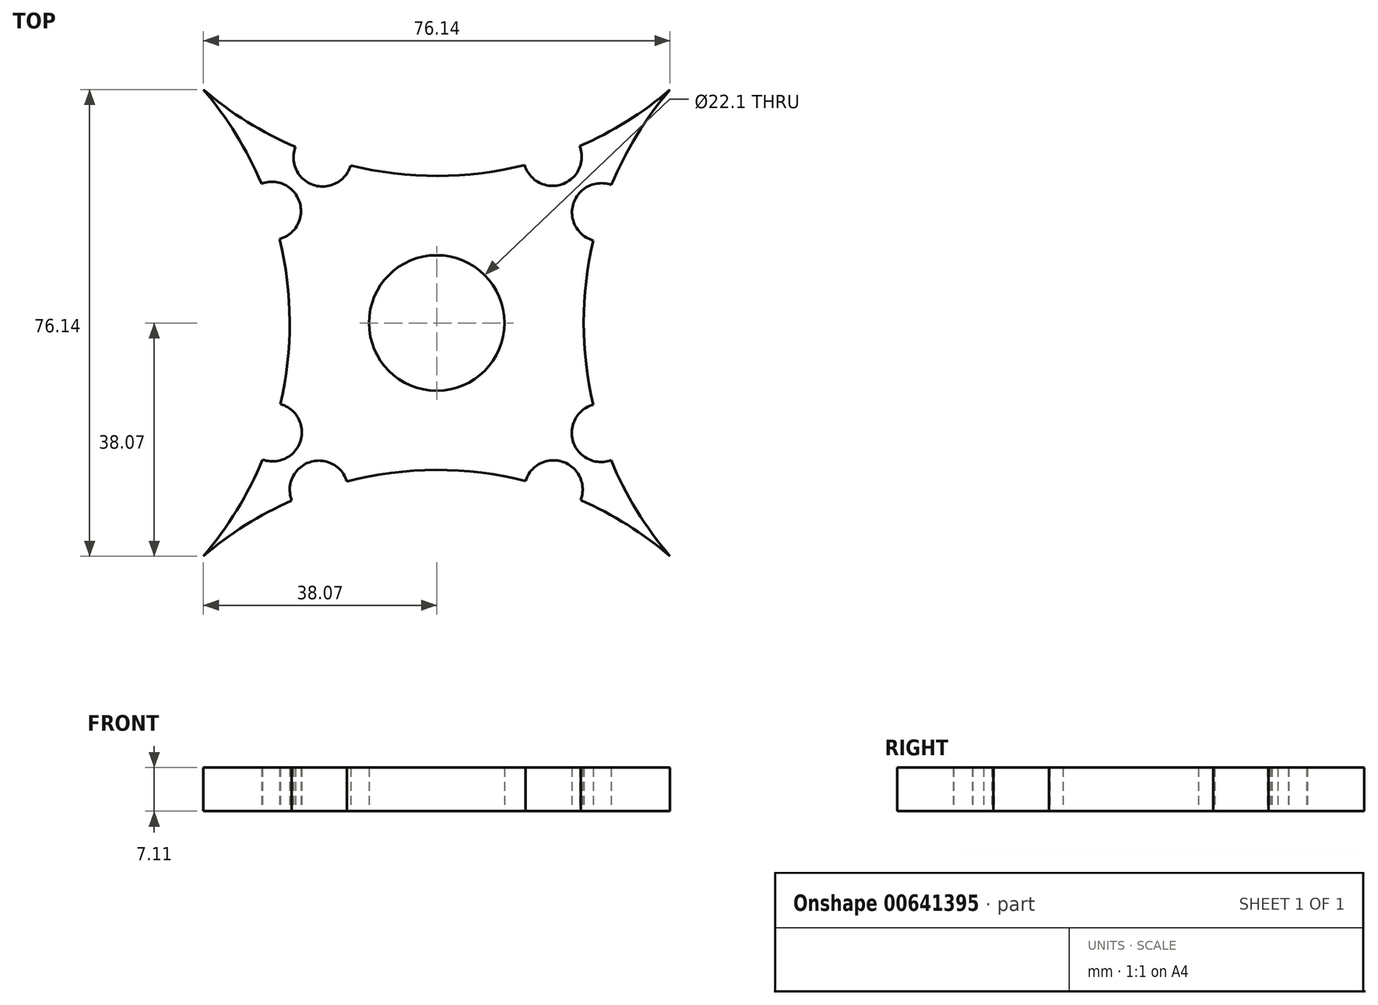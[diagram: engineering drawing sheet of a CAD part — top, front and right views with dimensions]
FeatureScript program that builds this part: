
annotation { "Feature Type Name" : "Feature", "Feature Type Description" : "" }
export const myFeature = defineFeature(function(context is Context, id is Id, definition is map)
    precondition{}
    {
        {
            var Q0;
            Q0=qCreatedBy(makeId("Top.planeOp"),FACE);
            var sketch = newSketch(context, id + "F0", { "sketchPlane" : qUnion([Q0])});
            skCircle(sketch, "E0", {"center": v(0, 0) * mm, "radius": 11.05 * mm});
            skLineSegment(sketch, "E1.bottom", {"start": v(-44.41, 44.41) * mm, "end": v(44.41, 44.41) * mm});
            skLineSegment(sketch, "E1.top", {"start": v(-44.41, -44.41) * mm, "end": v(44.41, -44.41) * mm});
            skLineSegment(sketch, "E1.left", {"start": v(-44.41, 44.41) * mm, "end": v(-44.41, -44.41) * mm});
            skLineSegment(sketch, "E1.right", {"start": v(44.41, 44.41) * mm, "end": v(44.41, -44.41) * mm});
            skArc(sketch, "E2", {"start": v(-44.41, 44.41) * mm, "mid": v(-34.64, 35.35) * mm, "end": v(-23.06, 28.73) * mm});
            skArc(sketch, "E3", {"start": v(44.41, 44.41) * mm, "mid": v(35.17, 34.4) * mm, "end": v(28.5, 22.5) * mm});
            skArc(sketch, "E4", {"start": v(44.41, -44.41) * mm, "mid": v(34.82, -35.48) * mm, "end": v(23.49, -28.91) * mm});
            skArc(sketch, "E5", {"start": v(-44.41, -44.41) * mm, "mid": v(-35.1, -34.3) * mm, "end": v(-28.4, -22.3) * mm});
            skArc(sketch, "E6", {"start": v(-25.61, 13.7) * mm, "mid": v(-22.4, 19.76) * mm, "end": v(-28.59, 22.73) * mm});
            skArc(sketch, "E7", {"start": v(-23.06, 28.73) * mm, "mid": v(-20.13, 22.51) * mm, "end": v(-14.04, 25.7) * mm});
            skArc(sketch, "E8", {"start": v(-28.4, -22.3) * mm, "mid": v(-22.23, -19.28) * mm, "end": v(-25.5, -13.24) * mm});
            skArc(sketch, "E9", {"start": v(-14.66, -25.85) * mm, "mid": v(-20.78, -22.74) * mm, "end": v(-23.64, -28.98) * mm});
            skArc(sketch, "E10", {"start": v(23.49, -28.91) * mm, "mid": v(20.6, -22.67) * mm, "end": v(14.5, -25.81) * mm});
            skArc(sketch, "E11", {"start": v(25.53, -13.35) * mm, "mid": v(22.27, -19.4) * mm, "end": v(28.45, -22.4) * mm});
            skArc(sketch, "E12", {"start": v(28.5, 22.5) * mm, "mid": v(22.3, 19.5) * mm, "end": v(25.56, 13.45) * mm});
            skArc(sketch, "E13", {"start": v(14.34, 25.77) * mm, "mid": v(20.44, 22.62) * mm, "end": v(23.34, 28.85) * mm});
            skArc(sketch, "E14.trimOffspring", {"start": v(-28.59, 22.73) * mm, "mid": v(-35.24, 34.5) * mm, "end": v(-44.41, 44.41) * mm});
            skArc(sketch, "E15.trimOffspring", {"start": v(-25.5, -13.24) * mm, "mid": v(-23.99, 0.23) * mm, "end": v(-25.61, 13.7) * mm});
            skArc(sketch, "E16.trimOffspring", {"start": v(-23.64, -28.98) * mm, "mid": v(-34.9, -35.53) * mm, "end": v(-44.41, -44.41) * mm});
            skArc(sketch, "E17.trimOffspring", {"start": v(14.5, -25.81) * mm, "mid": v(-0.09, -23.99) * mm, "end": v(-14.66, -25.85) * mm});
            skArc(sketch, "E18.trimOffspring", {"start": v(28.45, -22.4) * mm, "mid": v(35.13, -34.35) * mm, "end": v(44.41, -44.41) * mm});
            skArc(sketch, "E19.trimOffspring", {"start": v(25.56, 13.45) * mm, "mid": v(23.99, 0.05) * mm, "end": v(25.53, -13.35) * mm});
            skArc(sketch, "E20.trimOffspring", {"start": v(23.34, 28.85) * mm, "mid": v(34.76, 35.43) * mm, "end": v(44.41, 44.41) * mm});
            skArc(sketch, "E21.trimOffspring", {"start": v(-14.04, 25.7) * mm, "mid": v(0.15, 23.99) * mm, "end": v(14.34, 25.77) * mm});
            skSolve(sketch);
        }
        {
            var Q0;
            Q0=makeQuery(id+"F0.imprint","IMPRINT",FACE,{"disambiguationData":[TD([[makeQuery(id+"F0.imprint","IMPRINT",EDGE,{"derivedFrom":sQuery(id+"F0.wireOp",EDGE,"E0")}),-1.0]])]});
            extrude(context, id + "F1", {"entities" : qUnion([Q0]), "depth" : 7.11 * mm, "offsetDistance" : 25.4 * mm});
        }
    });
